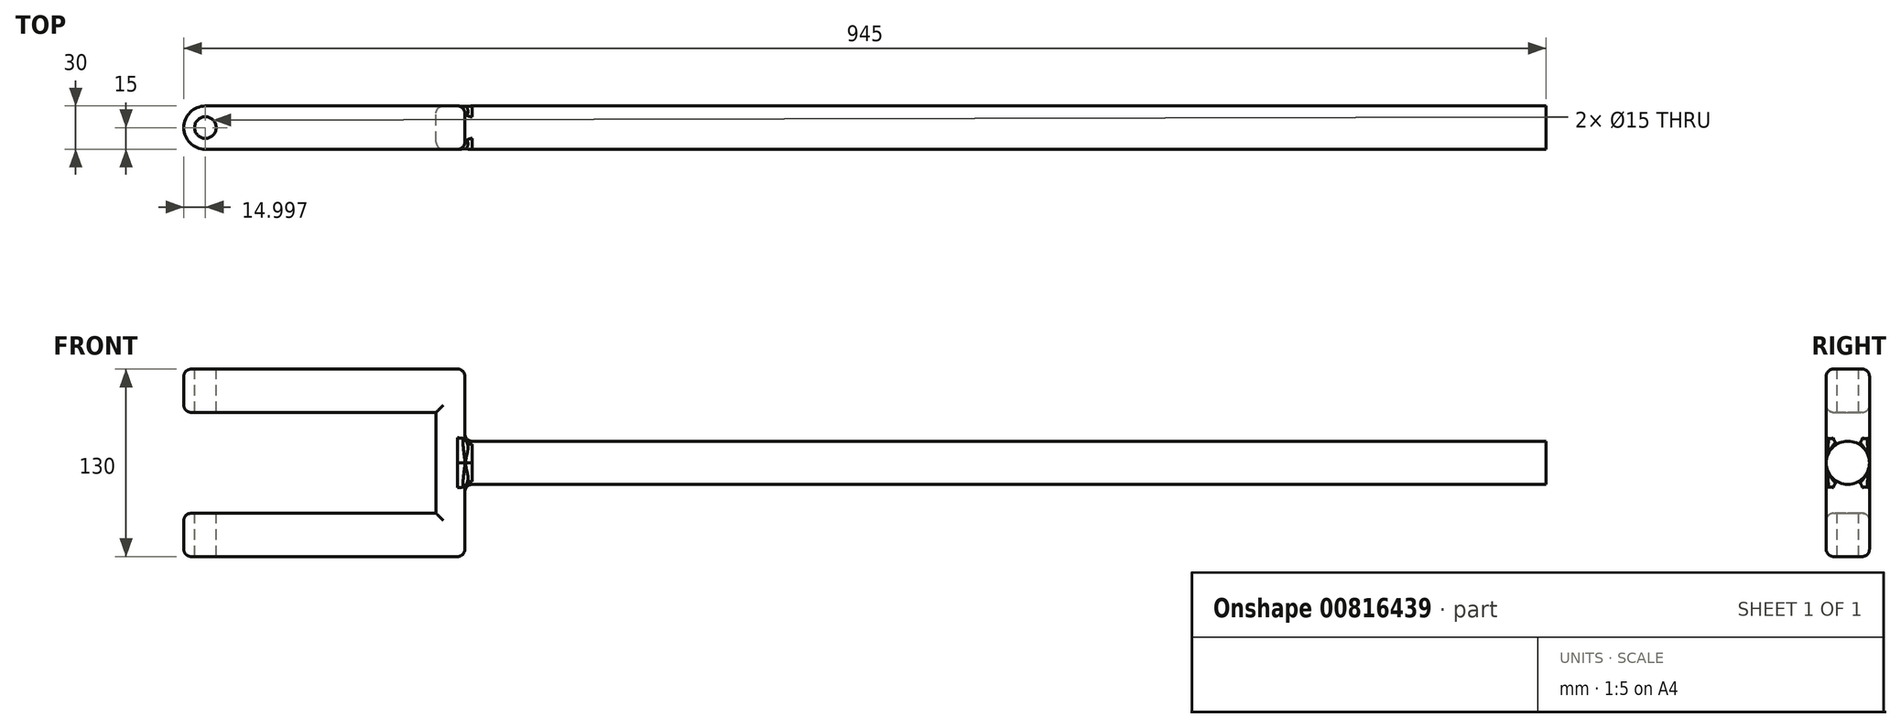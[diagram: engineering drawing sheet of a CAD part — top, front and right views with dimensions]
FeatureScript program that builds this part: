
annotation { "Feature Type Name" : "Feature", "Feature Type Description" : "" }
export const myFeature = defineFeature(function(context is Context, id is Id, definition is map)
    precondition{}
    {
        {
            var Q0;
            Q0=qCreatedBy(makeId("Front.planeOp"),FACE);
            var sketch = newSketch(context, id + "F0", { "sketchPlane" : qUnion([Q0])});
            skLineSegment(sketch, "E0.bottom", {"start": v(-124.32, 60) * mm, "end": v(70.68, 60) * mm});
            skLineSegment(sketch, "E0.top", {"start": v(-124.32, -70) * mm, "end": v(70.68, -70) * mm});
            skLineSegment(sketch, "E0.left", {"start": v(-124.32, 60) * mm, "end": v(-124.32, 30) * mm});
            skLineSegment(sketch, "E0.right", {"start": v(70.68, 60) * mm, "end": v(70.68, -70) * mm});
            skLineSegment(sketch, "E1.bottom", {"start": v(-124.32, 30) * mm, "end": v(50.68, 30) * mm});
            skLineSegment(sketch, "E1.top", {"start": v(-124.32, -40) * mm, "end": v(50.68, -40) * mm});
            skLineSegment(sketch, "E1.right", {"start": v(50.68, 30) * mm, "end": v(50.68, -40) * mm});
            skLineSegment(sketch, "E2.trimOffspring", {"start": v(-124.32, -40) * mm, "end": v(-124.32, -70) * mm});
            skLineSegment(sketch, "E3.top", {"start": v(70.68, -20) * mm, "end": v(820.68, -20) * mm});
            skLineSegment(sketch, "E3.left", {"start": v(70.68, 10) * mm, "end": v(70.68, -20) * mm});
            skLineSegment(sketch, "E3.right", {"start": v(820.68, -5) * mm, "end": v(820.68, -20) * mm});
            skLineSegment(sketch, "E4", {"start": v(820.68, -5) * mm, "end": v(70.68, -5) * mm});
            skPoint(sketch, "E5.orphan", {"position": v(820.68, 10) * mm});
            skSolve(sketch);
        }
        {
            var Q0;
            {var subQ1=sQuery(id+"F0.wireOp",EDGE,"E0.bottom");Q0=makeQuery(id+"F0.imprint","IMPRINT",FACE,{"disambiguationData":[TD([[makeQuery(id+"F0.imprint","IMPRINT",EDGE,{"derivedFrom":subQ1}),-1.0]])]});}
            extrude(context, id + "F1", {"entities" : qUnion([Q0]), "endBound" : BoundingType.SYMMETRIC, "depth" : 30 * mm, "offsetDistance" : 25 * mm});
        }
        {
            var Q0;
            {var subQ0=sQuery(id+"F0.wireOp",EDGE,"E3.top");Q0=makeQuery(id+"F0.imprint","IMPRINT",FACE,{"disambiguationData":[TD([[makeQuery(id+"F0.imprint","IMPRINT",EDGE,{"derivedFrom":subQ0}),1.0]])]});}
            var Q1;
            Q1=sQuery(id+"F0.wireOp",EDGE,"E4");
            revolve(context, id + "F2", {"operationType" : NewBodyOperationType.ADD, "surfaceOperationType" : NewSurfaceOperationType.NEW, "entities" : qUnion([Q0]), "axis" : qUnion([Q1]), "revolveType" : RevolveType.FULL});
        }
        {
            var Q0;
            Q0=makeQuery(id+"F1.opExtrude","SWEPT_FACE",FACE,{"disambiguationData":[OSD([sQuery(id+"F0.wireOp",EDGE,"E0.bottom")])]});
            var sketch = newSketch(context, id + "F3", { "sketchPlane" : qUnion([Q0])});
            skLineSegment(sketch, "E6.bottom", {"start": v(-109.32, 15) * mm, "end": v(70.68, 15) * mm});
            skLineSegment(sketch, "E6.top", {"start": v(-109.32, -15) * mm, "end": v(70.68, -15) * mm});
            skLineSegment(sketch, "E6.left", {"start": v(-124.32, 0) * mm, "end": v(-124.32, 0) * mm});
            skLineSegment(sketch, "E6.right", {"start": v(70.68, 15) * mm, "end": v(70.68, -15) * mm});
            skPoint(sketch, "E7.visualSharp", {"position": v(-124.32, 15) * mm});
            skArc(sketch, "E7.filletArc", {"start": v(-109.32, 15) * mm, "mid": v(-119.93, 10.6) * mm, "end": v(-124.32, 0) * mm});
            skPoint(sketch, "E8.visualSharp", {"position": v(-124.32, -15) * mm});
            skArc(sketch, "E8.filletArc", {"start": v(-124.32, 0) * mm, "mid": v(-119.93, -10.6) * mm, "end": v(-109.32, -15) * mm});
            skCircle(sketch, "E9", {"center": v(-109.32, 0) * mm, "radius": 7.5 * mm});
            skSolve(sketch);
        }
        {
            var Q0;
            Q0=makeQuery(id+"F3.imprint","IMPRINT",FACE,{"disambiguationData":[TD([[makeQuery(id+"F3.imprint","IMPRINT",EDGE,{"derivedFrom":sQuery(id+"F3.wireOp",EDGE,"E9")}),1.0]])]});
            extrude(context, id + "F4", {"entities" : qUnion([Q0]), "operationType" : NewBodyOperationType.REMOVE, "oppositeDirection" : true, "depth" : 134.8 * mm, "offsetDistance" : 25 * mm});
        }
        {
            var Q0;
            {var subQ0=sQuery(id+"F3.wireOp",EDGE,"E7.filletArc");Q0=makeQuery(id+"F3.imprint","IMPRINT",FACE,{"disambiguationData":[TD([[makeQuery(id+"F3.imprint","IMPRINT",EDGE,{"derivedFrom":subQ0}),-1.0]])]});}
            var Q1;
            {var subQ0=sQuery(id+"F3.wireOp",EDGE,"E8.filletArc");Q1=makeQuery(id+"F3.imprint","IMPRINT",FACE,{"disambiguationData":[TD([[makeQuery(id+"F3.imprint","IMPRINT",EDGE,{"derivedFrom":subQ0}),-1.0]])]});}
            extrude(context, id + "F5", {"entities" : qUnion([Q0, Q1]), "operationType" : NewBodyOperationType.REMOVE, "oppositeDirection" : true, "depth" : 145.9 * mm, "offsetDistance" : 25 * mm});
        }
        {
            var Q0;
            Q0=makeQuery(id+"F1.opExtrude","CAP_EDGE",EDGE,{"disambiguationData":[OSD([sQuery(id+"F0.wireOp",EDGE,"E0.top")])],"isStart":true});
            var Q1;
            Q1=makeQuery(id+"F1.opExtrude","CAP_FACE",FACE,{"disambiguationData":[OSD([sQuery(id+"F0.wireOp",EDGE,"E0.bottom"),sQuery(id+"F0.wireOp",EDGE,"E0.top"),sQuery(id+"F0.wireOp",EDGE,"E0.left"),sQuery(id+"F0.wireOp",EDGE,"E0.right"),sQuery(id+"F0.wireOp",EDGE,"E1.bottom"),sQuery(id+"F0.wireOp",EDGE,"E1.top"),sQuery(id+"F0.wireOp",EDGE,"E1.right"),sQuery(id+"F0.wireOp",EDGE,"E2.trimOffspring"),sQuery(id+"F0.wireOp",EDGE,"E3.left")])],"isStart":true});
            var Q2;
            Q2=makeQuery(id+"F1.opExtrude","CAP_FACE",FACE,{"disambiguationData":[OSD([sQuery(id+"F0.wireOp",EDGE,"E0.bottom"),sQuery(id+"F0.wireOp",EDGE,"E0.top"),sQuery(id+"F0.wireOp",EDGE,"E0.left"),sQuery(id+"F0.wireOp",EDGE,"E0.right"),sQuery(id+"F0.wireOp",EDGE,"E1.bottom"),sQuery(id+"F0.wireOp",EDGE,"E1.top"),sQuery(id+"F0.wireOp",EDGE,"E1.right"),sQuery(id+"F0.wireOp",EDGE,"E2.trimOffspring"),sQuery(id+"F0.wireOp",EDGE,"E3.left")])],"isStart":false});
            var Q3;
            Q3=makeQuery(id+"F2.boolean.opBoolean","SPLIT",EDGE,{"disambiguationData":[OD(1.0)],"derivedFrom":makeQuery(id+"F2.opRevolve","SWEPT_EDGE",EDGE,{"disambiguationData":[OSD([sQuery(id+"F0.wireOp",EDGE,"E0.right"),sQuery(id+"F0.wireOp",EDGE,"E3.top"),sQuery(id+"F0.wireOp",EDGE,"E3.left")])]})});
            var Q4;
            {var subQ0=sQuery(id+"F0.wireOp",EDGE,"E3.left");var subQ1=sQuery(id+"F0.wireOp",EDGE,"E0.right");var subQ2=makeQuery(id+"F1.opExtrude","SWEPT_FACE",FACE,{"disambiguationData":[OSD([subQ1,subQ0])]});var subQ3=sQuery(id+"F0.wireOp",EDGE,"E0.top");Q4=makeQuery(id+"F2.boolean.opBoolean","SPLIT",FACE,{"disambiguationData":[TD([makeQuery(id+"F1.opExtrude","SWEPT_FACE",FACE,{"disambiguationData":[OSD([subQ3])]})])],"derivedFrom":subQ2});}
            var Q5;
            {var subQ0=sQuery(id+"F0.wireOp",EDGE,"E3.left");var subQ5=sQuery(id+"F0.wireOp",EDGE,"E0.right");var subQ8=sQuery(id+"F0.wireOp",EDGE,"E0.bottom");var subQ9=makeQuery(id+"F1.opExtrude","SWEPT_FACE",FACE,{"disambiguationData":[OSD([subQ5,subQ0])]});Q5=makeQuery(id+"F2.boolean.opBoolean","SPLIT",FACE,{"disambiguationData":[TD([makeQuery(id+"F1.opExtrude","SWEPT_FACE",FACE,{"disambiguationData":[OSD([subQ8])]})])],"derivedFrom":subQ9});}
            fillet(context, id + "F6", {"entities" : qUnion([Q0, Q1, Q2, Q3, Q4, Q5]), "radius" : 5 * mm, "tangentPropagation" : true, "allowEdgeOverflow" : false});
        }
    });
